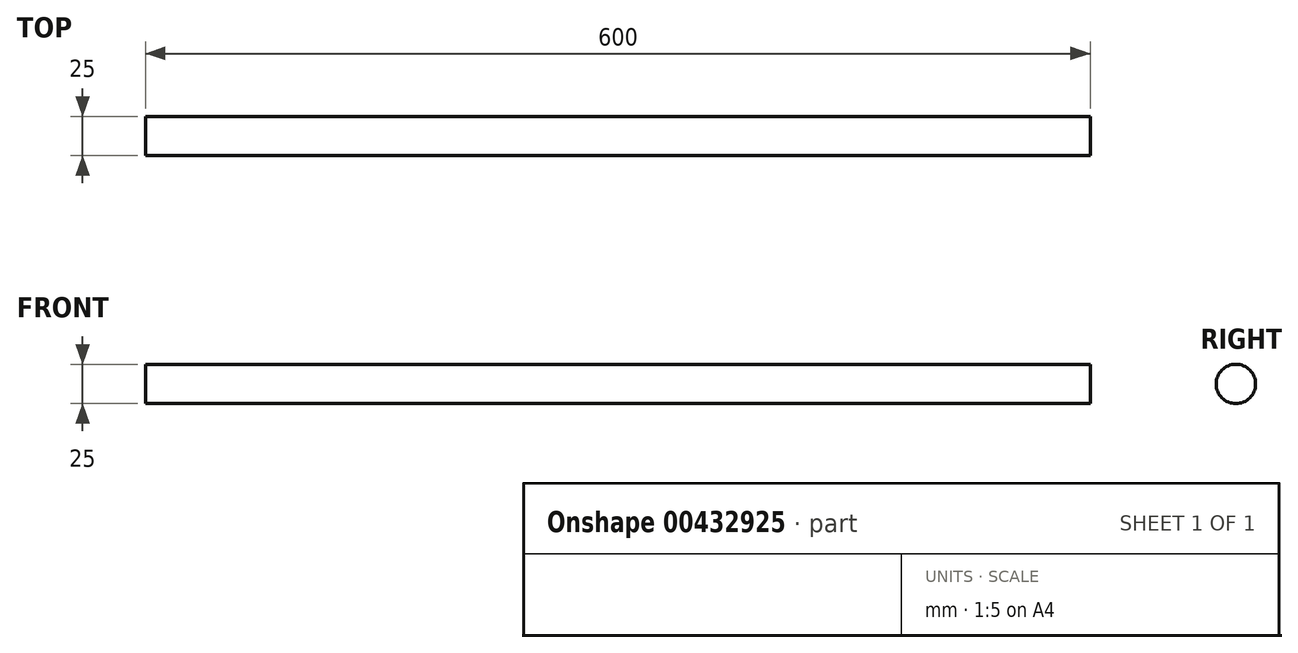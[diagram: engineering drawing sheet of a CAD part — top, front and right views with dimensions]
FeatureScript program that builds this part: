
annotation { "Feature Type Name" : "Feature", "Feature Type Description" : "" }
export const myFeature = defineFeature(function(context is Context, id is Id, definition is map)
    precondition{}
    {
        {
            var Q0;
            Q0=qCreatedBy(makeId("Right.planeOp"),FACE);
            var sketch = newSketch(context, id + "F0", { "sketchPlane" : qUnion([Q0])});
            skCircle(sketch, "E0", {"center": v(0, 0) * mm, "radius": 12.5 * mm});
            skSolve(sketch);
        }
        {
            var Q0;
            Q0=makeQuery(id+"F0.imprint","IMPRINT",FACE,{"disambiguationData":[TD([[makeQuery(id+"F0.imprint","IMPRINT",EDGE,{"derivedFrom":sQuery(id+"F0.wireOp",EDGE,"E0")}),1.0]])]});
            extrude(context, id + "F1", {"entities" : qUnion([Q0]), "depth" : 600 * mm});
        }
    });
